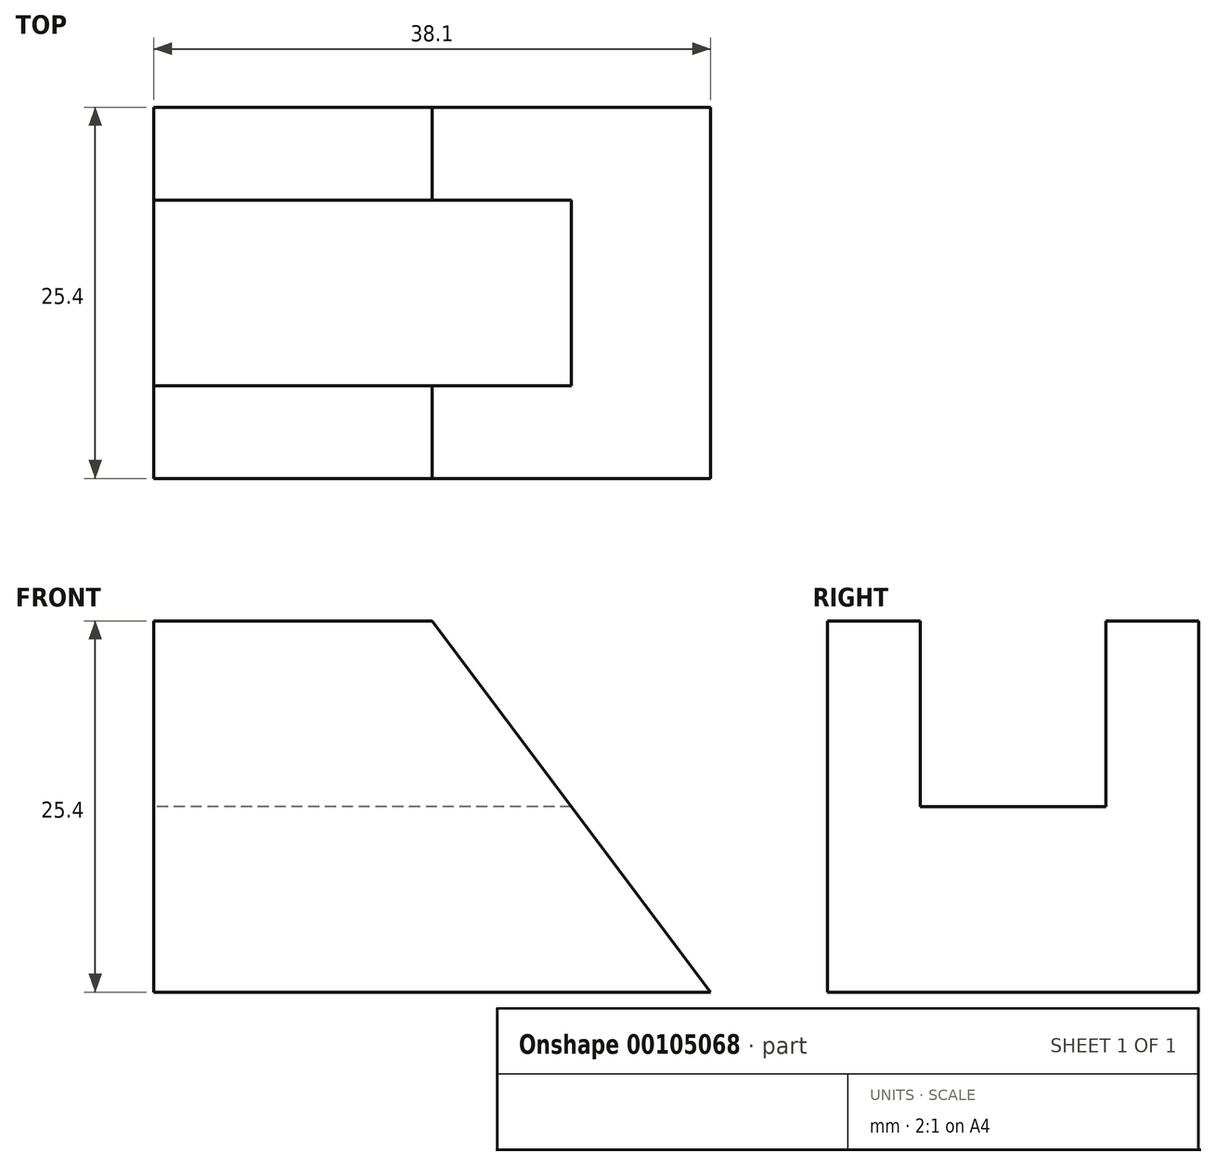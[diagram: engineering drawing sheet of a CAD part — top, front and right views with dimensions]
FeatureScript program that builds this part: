
annotation { "Feature Type Name" : "Feature", "Feature Type Description" : "" }
export const myFeature = defineFeature(function(context is Context, id is Id, definition is map)
    precondition{}
    {
        {
            var Q0;
            Q0=qCreatedBy(makeId("Right.planeOp"),FACE);
            var sketch = newSketch(context, id + "F0", { "sketchPlane" : qUnion([Q0])});
            skLineSegment(sketch, "E0", {"start": v(0, 0) * mm, "end": v(0, 25.4) * mm});
            skLineSegment(sketch, "E1", {"start": v(0, 25.4) * mm, "end": v(6.35, 25.4) * mm});
            skLineSegment(sketch, "E2", {"start": v(6.35, 25.4) * mm, "end": v(6.35, 12.7) * mm});
            skLineSegment(sketch, "E3", {"start": v(6.35, 12.7) * mm, "end": v(19.05, 12.7) * mm});
            skLineSegment(sketch, "E4", {"start": v(19.05, 12.7) * mm, "end": v(19.05, 25.4) * mm});
            skLineSegment(sketch, "E5", {"start": v(19.05, 25.4) * mm, "end": v(25.4, 25.4) * mm});
            skLineSegment(sketch, "E6", {"start": v(25.4, 25.4) * mm, "end": v(25.4, 0) * mm});
            skLineSegment(sketch, "E7", {"start": v(25.4, 0) * mm, "end": v(0, 0) * mm});
            skSolve(sketch);
        }
        {
            var Q0;
            Q0=qCreatedBy(makeId("Front.planeOp"),FACE);
            var sketch = newSketch(context, id + "F1", { "sketchPlane" : qUnion([Q0])});
            skLineSegment(sketch, "E8", {"start": v(0, 0) * mm, "end": v(0, 25.4) * mm});
            skLineSegment(sketch, "E9", {"start": v(0, 25.4) * mm, "end": v(19.05, 25.4) * mm});
            skLineSegment(sketch, "E10", {"start": v(19.05, 25.4) * mm, "end": v(38.1, 0) * mm});
            skLineSegment(sketch, "E11", {"start": v(38.1, 0) * mm, "end": v(0, 0) * mm});
            skLineSegment(sketch, "E12", {"start": v(19.05, 25.4) * mm, "end": v(38.1, 25.4) * mm});
            skLineSegment(sketch, "E13", {"start": v(38.1, 25.4) * mm, "end": v(38.1, 0) * mm});
            skSolve(sketch);
        }
        {
            var Q0;
            Q0=makeQuery(id+"F0.imprint","IMPRINT",FACE,{"disambiguationData":[TD([[makeQuery(id+"F0.imprint","IMPRINT",EDGE,{"derivedFrom":sQuery(id+"F0.wireOp",EDGE,"E0")}),-1.0]])]});
            extrude(context, id + "F2", {"entities" : qUnion([Q0]), "depth" : 38.1 * mm});
        }
        {
            var Q0;
            Q0=makeQuery(id+"F1.imprint","IMPRINT",FACE,{"disambiguationData":[TD([[makeQuery(id+"F1.imprint","IMPRINT",EDGE,{"derivedFrom":sQuery(id+"F1.wireOp",EDGE,"E10")}),1.0]])]});
            extrude(context, id + "F3", {"entities" : qUnion([Q0]), "operationType" : NewBodyOperationType.REMOVE, "endBound" : BoundingType.THROUGH_ALL, "oppositeDirection" : true, "depth" : 25.4 * mm});
        }
    });
